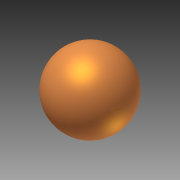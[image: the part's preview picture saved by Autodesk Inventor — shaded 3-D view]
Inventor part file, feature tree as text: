
AUTODESK INVENTOR PART (.ipt)
format: ipt  version: 2012 (Build 160160000, 160)  size: 101,376 bytes
history: native  units: in
note: dims shown in document units (in); Inventor stores cm internally (conversion verified against a paired STEP export)
features: revolve x1, sketch x1
ambient origin geometry x8: Origin, YZ Plane, XZ Plane, XY Plane, X Axis, Y Axis, Z Axis, Center Point
bodies: Solid1 (feature_tree)
feature tree (2):
  revolve  "Revolution1"  Angle=90.0deg
  sketch  "Sketch1"  dims[d0=8.0in d1=90.0deg]
